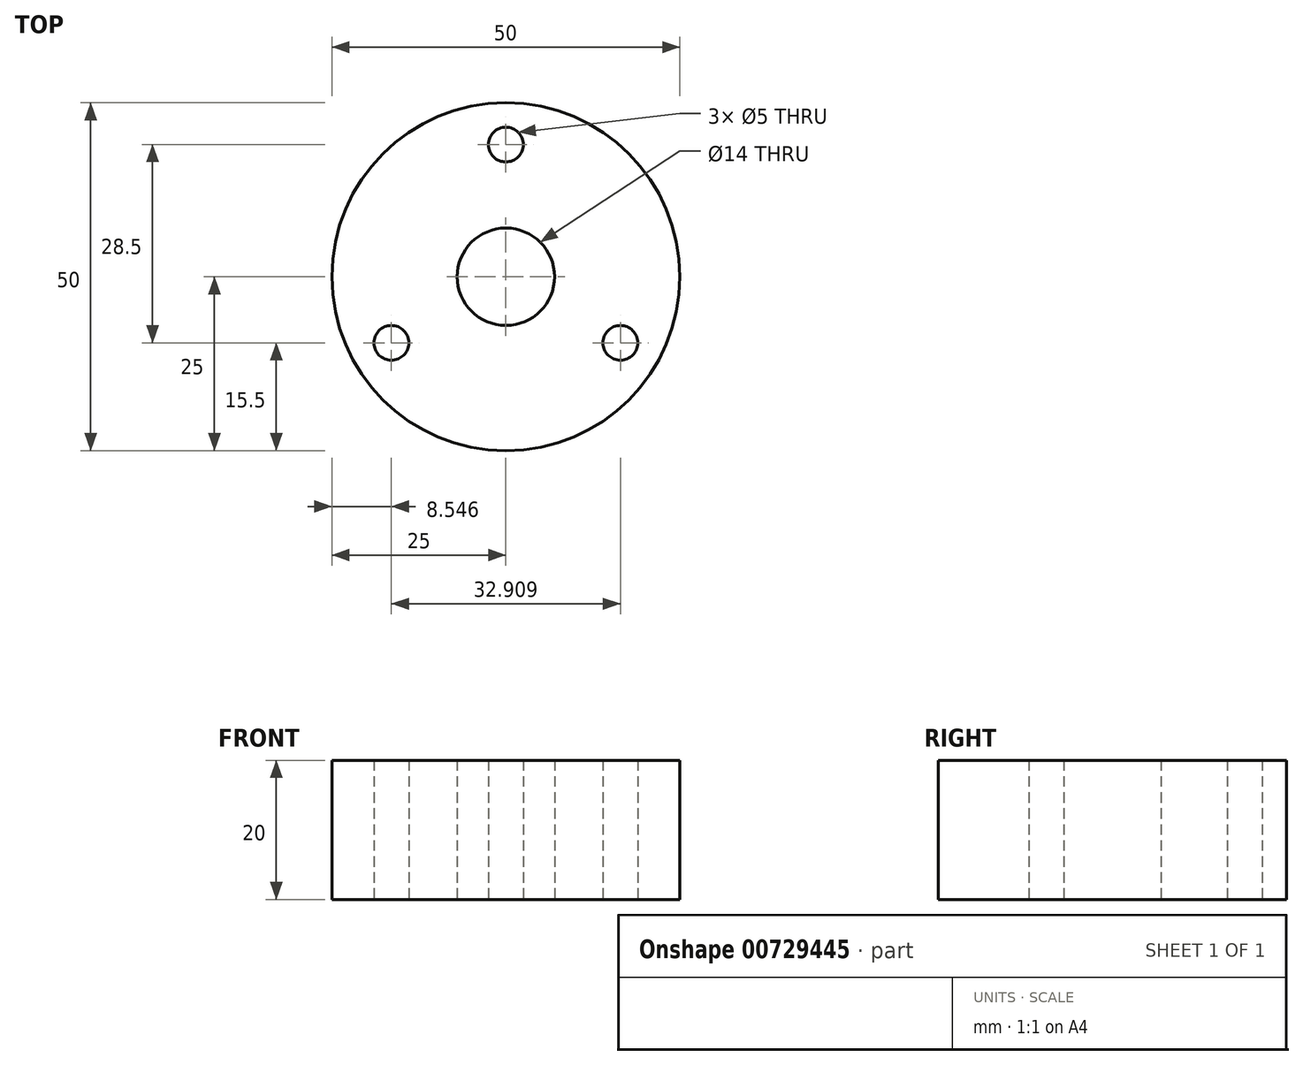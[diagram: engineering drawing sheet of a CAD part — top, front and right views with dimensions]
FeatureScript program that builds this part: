
annotation { "Feature Type Name" : "Feature", "Feature Type Description" : "" }
export const myFeature = defineFeature(function(context is Context, id is Id, definition is map)
    precondition{}
    {
        {
            var Q0;
            Q0=qCreatedBy(makeId("Top.planeOp"),FACE);
            var sketch = newSketch(context, id + "F0", { "sketchPlane" : qUnion([Q0])});
            skCircle(sketch, "E0", {"center": v(0, 0) * mm, "radius": 25 * mm});
            skCircle(sketch, "E1", {"center": v(0, 0) * mm, "radius": 7 * mm});
            skCircle(sketch, "E2", {"center": v(0, 19) * mm, "radius": 2.5 * mm});
            skCircle(sketch, "E3", {"center": v(16.45, -9.5) * mm, "radius": 2.5 * mm});
            skCircle(sketch, "E4", {"center": v(-16.45, -9.5) * mm, "radius": 2.5 * mm});
            skLineSegment(sketch, "E5", {"start": v(0, 0) * mm, "end": v(16.45, -9.5) * mm, "construction": true});
            skLineSegment(sketch, "E6", {"start": v(0, 0) * mm, "end": v(-16.45, -9.5) * mm, "construction": true});
            skLineSegment(sketch, "E7", {"start": v(0, 0) * mm, "end": v(0, 19) * mm, "construction": true});
            skSolve(sketch);
        }
        {
            var Q0;
            Q0=makeQuery(id+"F0.imprint","IMPRINT",FACE,{"disambiguationData":[TD([[makeQuery(id+"F0.imprint","IMPRINT",EDGE,{"derivedFrom":sQuery(id+"F0.wireOp",EDGE,"E0")}),1.0]])]});
            extrude(context, id + "F1", {"entities" : qUnion([Q0]), "depth" : 20 * mm, "offsetDistance" : 25 * mm});
        }
    });
